# Revit family: Power_Module-Lutron-GRAFIK_Eye-PHPMSW
name_source: partatom
category: Lighting Devices
revit_build: Autodesk Revit 2017 (Build: 20160720_1515(x64)
units: mm (PartAtom-declared; Revit-internal decimal feet)

## family parameters
Always vertical = No
Cut with Voids When Loaded = No
Maintain Annotation Orientation = No
OmniClass Number = 23.85.80.11.27
OmniClass Title = Lighting Controls
Part Type = Normal
Room Calculation Point = No
Round Connector Dimension = Use Diameter
Shared = No
Work Plane-Based = Yes

## types (1)
- PHPM-SW-DV-WH
    Assembly Code = D5020
    Capacity = 16 A
    Control Voltage = 120 V
    Cost = 0 $
    Default Elevation = 4' - 0"
    Description = Switching Power Module
    Instruction Sheet Link = http://www.lutron.com
    Label = PM
    Load Classification = Lighting
    Load Voltage = 277 V
    Manufacturer = Lutron Electronics Co., Inc
    Manufacturer Fax Number = 610-282-1243
    Model = PHPM-SW-DV-WH
    Number of Poles = 1
    Overall Depth = 0' - 1 19/32"
    Overall Height = 0' - 5 3/32"
    Overall Width = 0' - 6 5/16"
    Performance URL = http://www.lutron.com
    Power Module Material = Plastic - Lutron - White
    Product Documentation Link = http://www.lutron.com
    Product Name = Switching Power Module
    Product Page URL = http://www.lutron.com
    Series = GRAFIK Eye QS
    URL = http://www.lutron.com
    Version = 2017 - v1.0b
    Video Link = https://www.youtube.com
    Warranty URL = http://www.lutron.com

## geometry (parser evidence)
native form markers: Blend x4, Sweep x3
no freeform markers — native parametric forms only
